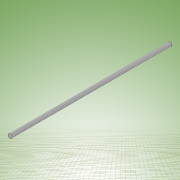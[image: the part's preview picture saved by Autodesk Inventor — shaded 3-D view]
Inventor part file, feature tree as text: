
AUTODESK INVENTOR PART (.ipt)
format: ipt  version: 2022 (Build 260153000, 153)  size: 111,104 bytes
history: native  units: mm
features: other x1, extrude x1, thread x1, sketch x1
ambient origin geometry x8: Origin, YZ Plane, XZ Plane, XY Plane, X Axis, Y Axis, Z Axis, Center Point
bodies: Body1 (feature_tree)
feature tree (4):
  other  "Sólido1"
  extrude  "Extrusión1"  Depth=250.0mm TaperAngle=0.0deg
  thread  "Rosca1"  [1 undecoded]
  sketch  "Boceto1"  dims[d0=6.35mm d1=250.0mm d2=0.0mm d3=200.0mm d4=0.0mm d5=0.5mm d6=0.872665mm d7=0.5mm d8=0.872665mm]
note: 1 required parameter value undecoded (feature->parameter linkage not recoverable at this tier; creation-order binding heuristic only, values carry confidence <= 0.55)
